# Revit family: FP-Revit20-en-OS30S_CombiSteamOven-0-90005523A-US-CA
name_source: partatom
category: Specialty Equipment
units: mm (PartAtom-declared; Revit-internal decimal feet)

## family parameters
Always vertical = Yes
Cut with Voids When Loaded = Yes
OmniClass Number = 23.40.40.14.17.11
OmniClass Title = Cookers, Ovens, Stoves
Part Type = Normal
Room Calculation Point = No
Round Connector Dimension = Use Diameter
Shared = No
Work Plane-Based = No

## types (6) — shared parameters
Cavity - Depth = 550 mm
Cavity - Height = 580 mm  [stored 1.90289 ft]
Cavity - Width = 724 mm  [stored 2.37533 ft]
Chassis - Depth = 545 mm  [stored 1.78806 ft]
Chassis - Height = 575 mm
Chassis - Width = 555 mm  [stored 1.82087 ft]
Connector Description - Electrical = 208 or 240 V, 60 Hz, 20 A circuit
Description = 30" Combination Steam Oven
Manufacturer = Fisher & Paykel Appliances
Material - Body = Fisher & Paykel - Grey
Material - Clearance Required = Fisher & Paykel - Clearance Required
Opening - Height = 600 mm
Opening - Width = 762 mm  [stored 2.5 ft]
Product - Height = 598 mm  [stored 1.96194 ft]
Product - Width = 758 mm  [stored 2.48688 ft]
URL = www.fisherpaykel.com
zero-valued in all types: Default Elevation

## per-type parameters (varying)
| type | Control Panel - Depth | Opening - Depth | Product - Depth | Style | Type Comments |
| OS30SPUX3 | 24 mm  [stored 0.0787402 ft] | 24 mm  [stored 0.0787402 ft] | 569 mm | 30in-76cm Fronts : 30in Front Professional | Professional, Stainless |
| OS30SMUB3 | 20 mm  [stored 0.0656168 ft] | 20 mm  [stored 0.0656168 ft] | 565 mm | 30in-76cm Fronts : 30in Front Minimal (Black) | Minimal, Black |
| OS30SMUG3 | 20 mm  [stored 0.0656168 ft] | 20 mm  [stored 0.0656168 ft] | 565 mm | 30in-76cm Fronts : 30in Front Minimal (Grey) | Minimal, Grey |
| OS30SMUNB3 | 20 mm  [stored 0.0656168 ft] | 20 mm  [stored 0.0656168 ft] | 565 mm | 30in-76cm Fronts : 30in Front Minimal (Black) No Handle | Minimal, Black, Handleless |
| OS30SMUNG3 | 20 mm  [stored 0.0656168 ft] | 20 mm  [stored 0.0656168 ft] | 565 mm | 30in-76cm Fronts : 30in Front Minimal (Grey) No Handle | Minimal, Grey, Handleless |
| OS30SCUDX3 | 20 mm  [stored 0.0656168 ft] | 20 mm  [stored 0.0656168 ft] | 565 mm | 30in-76cm Fronts : 30in Front Contemporary w Dial (Stainless) | Contemporary, Stainless |

note: column(s) folded — value = type name in every type: Model

note: [stored X ft] marks values corroborated as IEEE doubles in the binary element streams (Revit-internal decimal feet)

## geometry (parser evidence)
native form markers: Sweep x16
no freeform markers — native parametric forms only
